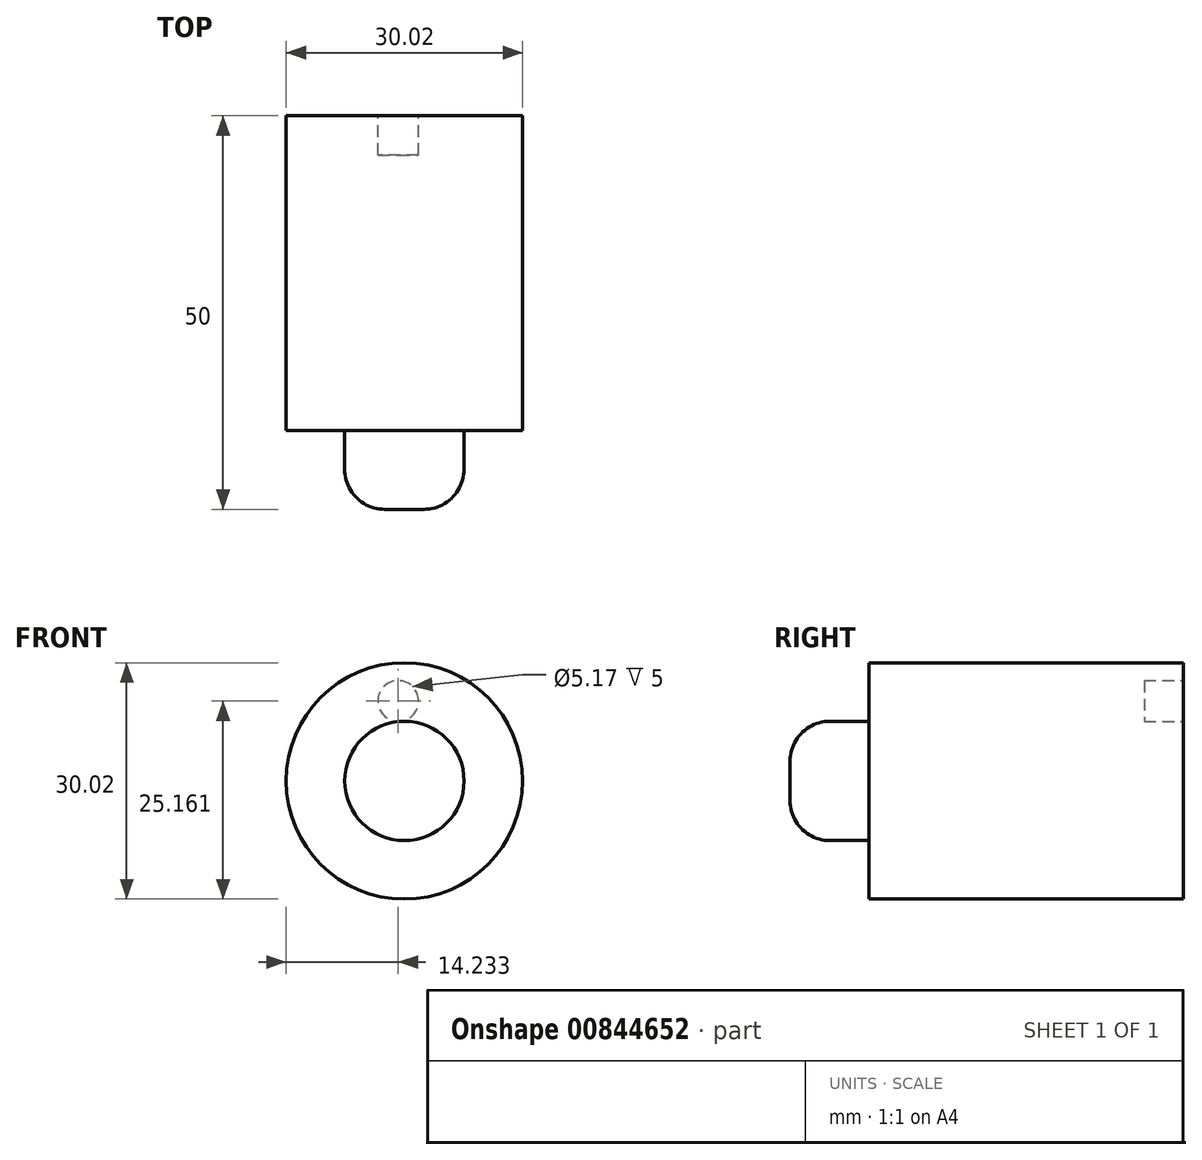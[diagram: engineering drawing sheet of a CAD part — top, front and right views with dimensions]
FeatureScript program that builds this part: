
annotation { "Feature Type Name" : "Feature", "Feature Type Description" : "" }
export const myFeature = defineFeature(function(context is Context, id is Id, definition is map)
    precondition{}
    {
        {
            var Q0;
            Q0=qCreatedBy(makeId("Front.planeOp"),FACE);
            var sketch = newSketch(context, id + "F0", { "sketchPlane" : qUnion([Q0])});
            skCircle(sketch, "E0", {"center": v(0.78, -15) * mm, "radius": 15.01 * mm});
            skPoint(sketch, "E0.first.point", {"position": v(0, 0) * mm});
            skPoint(sketch, "E0.second.point", {"position": v(15.79, -15.13) * mm});
            skPoint(sketch, "E0.third.point", {"position": v(12.87, -23.89) * mm});
            skSolve(sketch);
        }
        {
            var Q0;
            Q0=makeQuery(id+"F0.imprint","IMPRINT",FACE,{"disambiguationData":[TD([[makeQuery(id+"F0.imprint","IMPRINT",EDGE,{"derivedFrom":sQuery(id+"F0.wireOp",EDGE,"E0")}),1.0]])]});
            extrude(context, id + "F1", {"entities" : qUnion([Q0]), "depth" : 40 * mm, "offsetDistance" : 25.4 * mm});
        }
        {
            var Q0;
            Q0=makeQuery(id+"F1.opExtrude","CAP_FACE",FACE,{"disambiguationData":[OSD([sQuery(id+"F0.wireOp",EDGE,"E0")])],"isStart":true});
            var sketch = newSketch(context, id + "F2", { "sketchPlane" : qUnion([Q0])});
            skCircle(sketch, "E1", {"center": v(0, -4.84) * mm, "radius": 2.59 * mm});
            skPoint(sketch, "E1.first.point", {"position": v(2.26, -6.1) * mm});
            skPoint(sketch, "E1.second.point", {"position": v(-2.52, -4.24) * mm});
            skPoint(sketch, "E1.third.point", {"position": v(-2, -3.18) * mm});
            skSolve(sketch);
        }
        {
            var Q0;
            Q0=makeQuery(id+"F2.imprint","IMPRINT",FACE,{"disambiguationData":[TD([[makeQuery(id+"F2.imprint","IMPRINT",EDGE,{"derivedFrom":sQuery(id+"F2.wireOp",EDGE,"E1")}),1.0]])]});
            extrude(context, id + "F3", {"entities" : qUnion([Q0]), "operationType" : NewBodyOperationType.REMOVE, "oppositeDirection" : true, "depth" : 5 * mm, "offsetDistance" : 25.4 * mm});
        }
        {
            var Q0;
            Q0=makeQuery(id+"F1.opExtrude","CAP_FACE",FACE,{"disambiguationData":[OSD([sQuery(id+"F0.wireOp",EDGE,"E0")])],"isStart":false});
            var sketch = newSketch(context, id + "F4", { "sketchPlane" : qUnion([Q0])});
            skCircle(sketch, "E2", {"center": v(0.78, -15) * mm, "radius": 7.58 * mm});
            skSolve(sketch);
        }
        {
            var Q0;
            Q0=makeQuery(id+"F4.imprint","IMPRINT",FACE,{"disambiguationData":[TD([[makeQuery(id+"F4.imprint","IMPRINT",EDGE,{"derivedFrom":sQuery(id+"F4.wireOp",EDGE,"E2")}),1.0]])]});
            extrude(context, id + "F5", {"entities" : qUnion([Q0]), "operationType" : NewBodyOperationType.ADD, "depth" : 10 * mm, "offsetDistance" : 25.4 * mm});
        }
        {
            var Q0;
            Q0=makeQuery(id+"F5.opExtrude","CAP_EDGE",EDGE,{"disambiguationData":[OSD([sQuery(id+"F4.wireOp",EDGE,"E2")])],"isStart":false});
            fillet(context, id + "F6", {"entities" : qUnion([Q0]), "radius" : 5.08 * mm, "tangentPropagation" : true, "allowEdgeOverflow" : false});
        }
    });
